# Revit family: ащк гзвфеу_42004XXX_туц
name_source: partatom
category: Plumbing Fixtures
revit_build: Autodesk Revit 2018 (Build: 20170223_1515(x64)
units: mm (PartAtom-declared; Revit-internal decimal feet)

## family parameters
Cut with Voids When Loaded = Yes
Host = Face
OmniClass Number = 23.31.13.00
OmniClass Title = Sinks
Part Type = Normal
Room Calculation Point = No
Round Connector Dimension = Use Diameter
Shared = No

## types (5) — shared parameters
Always visible = Yes
BIMobject category = Wash basins
Connector Description = Water Outlet 46 mm
Default Elevation = 1219 mm
Description = AXOR Universal Basins & Bathtubs Wash bowl 600/400 without tap hole and overflow
Design country = Germany
Diameter = 46 mm  [stored 0.150919 ft]
Edition number = 1
IFC Classification = Sanitary Terminal
Manufacturer = AXOR
Manufacturer country = Germany
Manufacturer name = AXOR
Masterformat 2014 Code = 22 41 39
Masterformat 2014 Description = Residential Faucets, Supplies, and Trim
Material = AXOR - Ceramic - White
Model = 42004XXX
OmniClass Code = 23-31 13 00
OmniClass Description = Sinks
Product Guid = 450b69f8-fd73-43bf-b088-0d01da95dfce
Product SKU = 42004XXX
Product data url = https://bimobject.com
Product family = AXOR Universal Basins & Bathtub
Product group = Washbasin
Product name = 42004XXX AXOR Universal Basins & Bathtubs Wash bowl 600/400 without tap hole and overflow
Product url = https://www.axor-design.com
QR code = https://bimobject.com
UNSPSC Code = 301815
URL = https://www.axor-design.com
Uniclass 2015 Code = Pr_40_20_87
Uniclass 2015 Name = Taps and water supply outlet fittings
Uniformat II Code = D2010
Uniformat II Description = Plumbing Fixtures
Version = 1
Weight Net (Kg) = 2.4

## per-type parameters (varying)
| type | Material 1 |
| 000 Chrome | AXOR - Metal - 000 Chrome |
| 140 Brushed Bronze | AXOR - Metal - 140 Brushed Bronze |
| 340 Brushed Black Chrome | AXOR - Metal - 340 Brushed Black Chrome |
| 670 Matte Black | AXOR - Metal - 670 Matte Black |
| 990 Polished Gold Optic | AXOR - Metal - 990 Polished Gold Optic |

note: [stored X ft] marks values corroborated as IEEE doubles in the binary element streams (Revit-internal decimal feet)

## geometry (parser evidence)
native form markers: Sweep x2
no freeform markers — native parametric forms only
